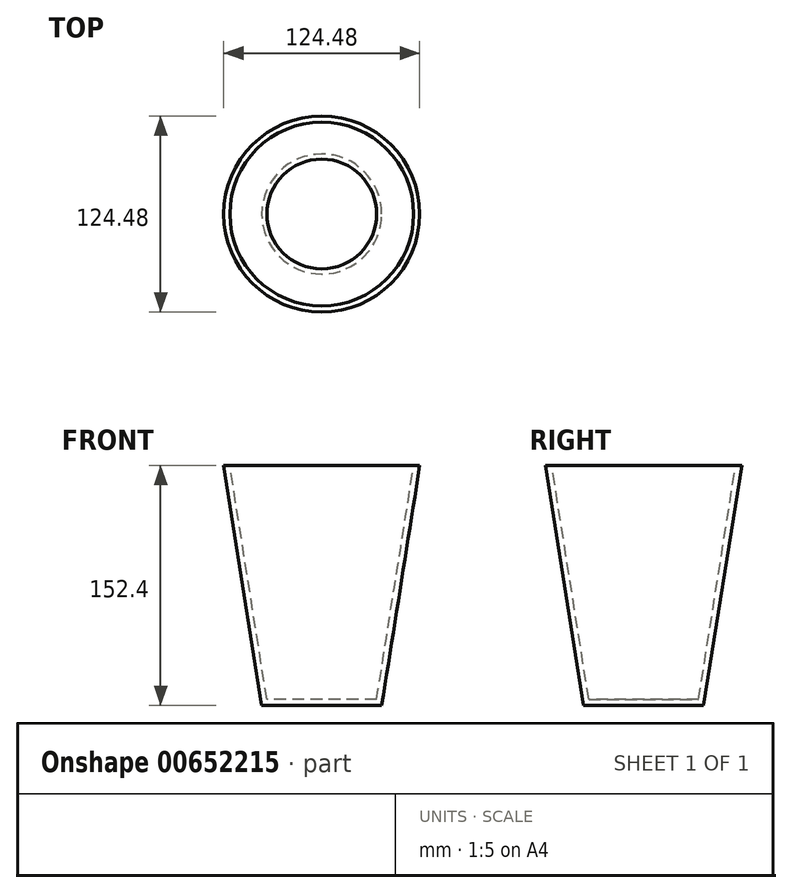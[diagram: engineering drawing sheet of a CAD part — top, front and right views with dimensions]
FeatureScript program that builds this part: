
annotation { "Feature Type Name" : "Feature", "Feature Type Description" : "" }
export const myFeature = defineFeature(function(context is Context, id is Id, definition is map)
    precondition{}
    {
        {
            var Q0;
            Q0=qCreatedBy(makeId("Top.planeOp"),FACE);
            var sketch = newSketch(context, id + "F0", { "sketchPlane" : qUnion([Q0])});
            skCircle(sketch, "E0", {"center": v(0, 0) * mm, "radius": 38.1 * mm});
            skSolve(sketch);
        }
        {
            var Q0;
            Q0=makeQuery(id+"F0.imprint","IMPRINT",FACE,{"disambiguationData":[TD([[makeQuery(id+"F0.imprint","IMPRINT",EDGE,{"derivedFrom":sQuery(id+"F0.wireOp",EDGE,"E0")}),1.0]])]});
            extrude(context, id + "F1", {"entities" : qUnion([Q0]), "depth" : 152.4 * mm, "offsetDistance" : 25.4 * mm, "hasDraft" : true, "draftAngle" : 9 * degree});
        }
        {
            var Q0;
            Q0=makeQuery(id+"F1.opExtrude","CAP_FACE",FACE,{"disambiguationData":[OSD([sQuery(id+"F0.wireOp",EDGE,"E0")])],"isStart":false});
            shell(context, id + "F2", {"entities" : qUnion([Q0]), "thickness" : 3.8 * mm});
        }
    });
